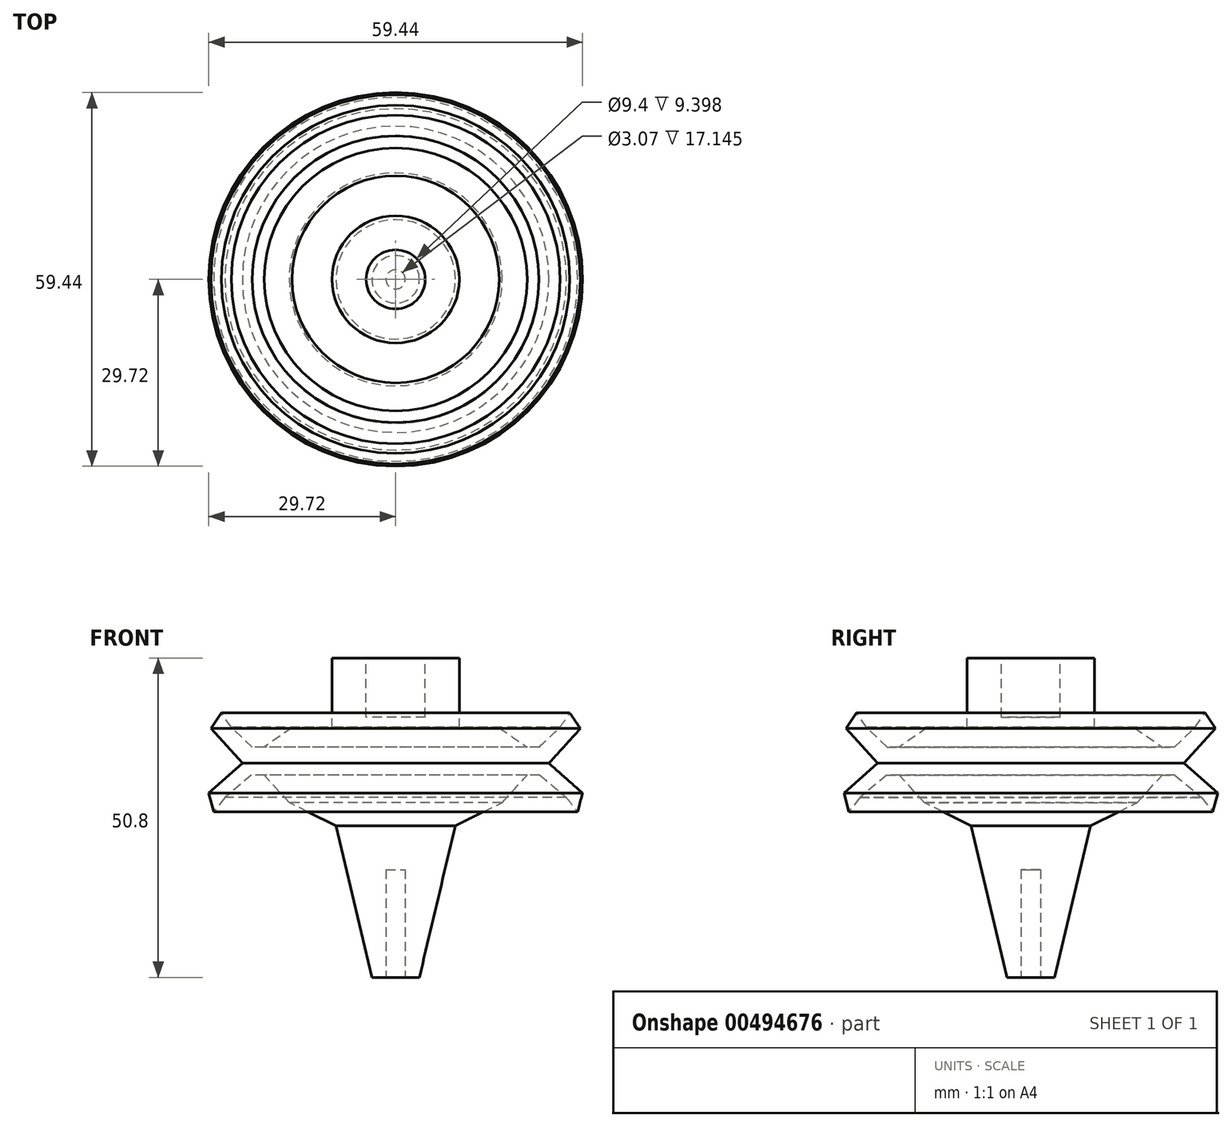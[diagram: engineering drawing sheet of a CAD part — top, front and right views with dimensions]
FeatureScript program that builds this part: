
annotation { "Feature Type Name" : "Feature", "Feature Type Description" : "" }
export const myFeature = defineFeature(function(context is Context, id is Id, definition is map)
    precondition{}
    {
        {
            var Q0;
            Q0=qCreatedBy(makeId("Front.planeOp"),FACE);
            var sketch = newSketch(context, id + "F0", { "sketchPlane" : qUnion([Q0])});
            skLineSegment(sketch, "E0", {"start": v(0, -12.49) * mm, "end": v(3.78, -12.49) * mm});
            skLineSegment(sketch, "E1", {"start": v(3.78, -12.49) * mm, "end": v(9.5, 11.63) * mm});
            skLineSegment(sketch, "E2", {"start": v(20.91, 19.68) * mm, "end": v(22.91, 19.68) * mm});
            skLineSegment(sketch, "E3", {"start": v(22.91, 19.68) * mm, "end": v(27.15, 16.12) * mm});
            skLineSegment(sketch, "E4", {"start": v(20.91, 24.14) * mm, "end": v(22.8, 24.14) * mm});
            skLineSegment(sketch, "E5", {"start": v(22.8, 24.14) * mm, "end": v(26.14, 27.29) * mm});
            skLineSegment(sketch, "E6", {"start": v(20.91, 24.14) * mm, "end": v(16.48, 27.2) * mm});
            skLineSegment(sketch, "E7", {"start": v(10.13, 27.2) * mm, "end": v(10.13, 38.31) * mm});
            skLineSegment(sketch, "E8", {"start": v(0, 27.88) * mm, "end": v(0, -12.49) * mm});
            skLineSegment(sketch, "E9", {"start": v(20.91, 19.68) * mm, "end": v(16.93, 15.33) * mm});
            skLineSegment(sketch, "E10", {"start": v(9.5, 11.63) * mm, "end": v(16.93, 15.33) * mm});
            skLineSegment(sketch, "E11", {"start": v(29.72, 16.81) * mm, "end": v(28.94, 13.86) * mm});
            skLineSegment(sketch, "E12", {"start": v(27.15, 16.12) * mm, "end": v(28.94, 13.86) * mm});
            skLineSegment(sketch, "E13", {"start": v(27.69, 29.57) * mm, "end": v(26.14, 27.29) * mm});
            skLineSegment(sketch, "E14", {"start": v(29.37, 27.08) * mm, "end": v(27.69, 29.57) * mm});
            skLineSegment(sketch, "E15", {"start": v(29.72, 16.81) * mm, "end": v(24.37, 21.56) * mm});
            skLineSegment(sketch, "E16", {"start": v(24.37, 21.56) * mm, "end": v(29.37, 27.08) * mm});
            skLineSegment(sketch, "E17", {"start": v(16.48, 27.2) * mm, "end": v(10.13, 27.2) * mm});
            skLineSegment(sketch, "E18", {"start": v(0, 38.31) * mm, "end": v(10.13, 38.31) * mm});
            skLineSegment(sketch, "E19", {"start": v(0, 38.31) * mm, "end": v(0, -12.49) * mm});
            skPoint(sketch, "E20", {"position": v(0, 38.31) * mm});
            skSolve(sketch);
        }
        {
            var Q0;
            {var subQ0=sQuery(id+"F0.wireOp",EDGE,"E0");Q0=makeQuery(id+"F0.imprint","IMPRINT",FACE,{"disambiguationData":[TD([[makeQuery(id+"F0.imprint","IMPRINT",EDGE,{"derivedFrom":subQ0}),1.0]])]});}
            var Q1;
            Q1=makeQuery(id+"F0.imprint","IMPRINT",FACE,{"disambiguationData":[TD([[makeQuery(id+"F0.imprint","IMPRINT",EDGE,{"derivedFrom":sQuery(id+"F0.wireOp",EDGE,"Yl4YsOVS-YFRs-yTc0-dnrn-sKbtm2UrnZcL")}),1.0]])]});
            var Q2;
            Q2=makeQuery(id+"F0.imprint","IMPRINT",FACE,{"disambiguationData":[TD([[makeQuery(id+"F0.imprint","IMPRINT",EDGE,{"derivedFrom":sQuery(id+"F0.wireOp",EDGE,"CABWVyWm-XD6T-IB5M-2arz-Lb2e3lOBGgFA")}),1.0]])]});
            var Q3;
            Q3=sQuery(id+"F0.wireOp",EDGE,"E8");
            revolve(context, id + "F1", {"entities" : qUnion([Q0, Q1, Q2]), "axis" : qUnion([Q3]), "revolveType" : RevolveType.FULL});
        }
        {
            var Q0;
            Q0=makeQuery(id+"F1.opRevolve","SWEPT_FACE",FACE,{"disambiguationData":[OSD([sQuery(id+"F0.wireOp",EDGE,"E18")])]});
            var sketch = newSketch(context, id + "F2", { "sketchPlane" : qUnion([Q0])});
            skCircle(sketch, "E21", {"center": v(0, 0) * mm, "radius": 4.7 * mm});
            skSolve(sketch);
        }
        {
            var Q0;
            Q0=makeQuery(id+"F2.imprint","IMPRINT",FACE,{"disambiguationData":[TD([[makeQuery(id+"F2.imprint","IMPRINT",EDGE,{"derivedFrom":sQuery(id+"F2.wireOp",EDGE,"E21")}),1.0]])]});
            extrude(context, id + "F3", {"entities" : qUnion([Q0]), "operationType" : NewBodyOperationType.REMOVE, "oppositeDirection" : true, "depth" : 9.4 * mm});
        }
        {
            var Q0;
            Q0=makeQuery(id+"F1.opRevolve","SWEPT_FACE",FACE,{"disambiguationData":[OSD([sQuery(id+"F0.wireOp",EDGE,"E0")])]});
            var sketch = newSketch(context, id + "F4", { "sketchPlane" : qUnion([Q0])});
            skCircle(sketch, "E22", {"center": v(0, 0) * mm, "radius": 1.54 * mm});
            skSolve(sketch);
        }
        {
            var Q0;
            Q0=makeQuery(id+"F4.imprint","IMPRINT",FACE,{"disambiguationData":[TD([[makeQuery(id+"F4.imprint","IMPRINT",EDGE,{"derivedFrom":sQuery(id+"F4.wireOp",EDGE,"E22")}),1.0]])]});
            extrude(context, id + "F5", {"entities" : qUnion([Q0]), "operationType" : NewBodyOperationType.REMOVE, "oppositeDirection" : true, "depth" : 17.14 * mm});
        }
    });
